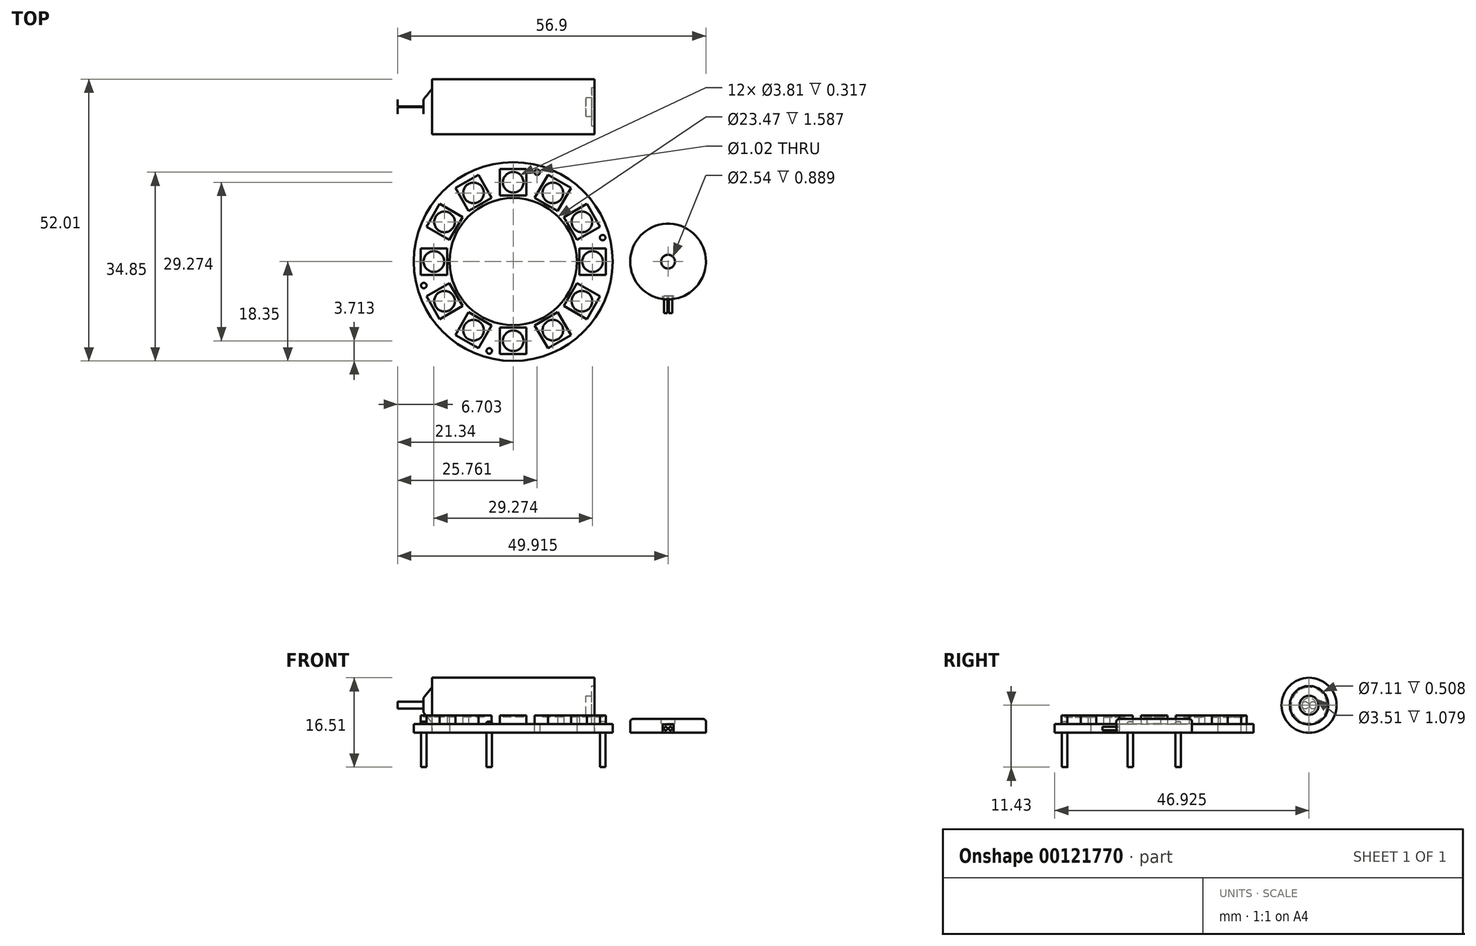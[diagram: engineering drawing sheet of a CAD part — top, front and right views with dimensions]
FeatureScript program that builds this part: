
annotation { "Feature Type Name" : "Feature", "Feature Type Description" : "" }
export const myFeature = defineFeature(function(context is Context, id is Id, definition is map)
    precondition{}
    {
        {
            var Q0;
            Q0=qCreatedBy(makeId("Top.planeOp"),FACE);
            var sketch = newSketch(context, id + "F0", { "sketchPlane" : qUnion([Q0])});
            skCircle(sketch, "E0", {"center": v(0, 0) * mm, "radius": 18.35 * mm});
            skCircle(sketch, "E1", {"center": v(0, 0) * mm, "radius": 11.73 * mm});
            skLineSegment(sketch, "E2", {"start": v(0, 0) * mm, "end": v(0, 18.35) * mm, "construction": true});
            skLineSegment(sketch, "E3.1.0", {"start": v(0, 0) * mm, "end": v(-4.75, 17.73) * mm, "construction": true});
            skLineSegment(sketch, "E3.2.0", {"start": v(0, 0) * mm, "end": v(-9.18, 15.9) * mm, "construction": true});
            skLineSegment(sketch, "E3.3.0", {"start": v(0, 0) * mm, "end": v(-12.98, 12.98) * mm, "construction": true});
            skLineSegment(sketch, "E3.4.0", {"start": v(0, 0) * mm, "end": v(-15.9, 9.18) * mm, "construction": true});
            skLineSegment(sketch, "E3.5.0", {"start": v(0, 0) * mm, "end": v(-17.73, 4.75) * mm, "construction": true});
            skLineSegment(sketch, "E3.6.0", {"start": v(0, 0) * mm, "end": v(-18.35, 0) * mm, "construction": true});
            skLineSegment(sketch, "E3.7.0", {"start": v(0, 0) * mm, "end": v(-17.73, -4.75) * mm, "construction": true});
            skLineSegment(sketch, "E3.8.0", {"start": v(0, 0) * mm, "end": v(-15.9, -9.18) * mm, "construction": true});
            skLineSegment(sketch, "E3.9.0", {"start": v(0, 0) * mm, "end": v(-12.98, -12.98) * mm, "construction": true});
            skLineSegment(sketch, "E3.10.0", {"start": v(0, 0) * mm, "end": v(-9.18, -15.9) * mm, "construction": true});
            skLineSegment(sketch, "E3.11.0", {"start": v(0, 0) * mm, "end": v(-4.75, -17.73) * mm, "construction": true});
            skLineSegment(sketch, "E3.12.0", {"start": v(0, 0) * mm, "end": v(0, -18.35) * mm, "construction": true});
            skLineSegment(sketch, "E3.13.0", {"start": v(0, 0) * mm, "end": v(4.75, -17.73) * mm, "construction": true});
            skLineSegment(sketch, "E3.14.0", {"start": v(0, 0) * mm, "end": v(9.18, -15.9) * mm, "construction": true});
            skLineSegment(sketch, "E3.15.0", {"start": v(0, 0) * mm, "end": v(12.98, -12.98) * mm, "construction": true});
            skLineSegment(sketch, "E3.16.0", {"start": v(0, 0) * mm, "end": v(15.9, -9.18) * mm, "construction": true});
            skLineSegment(sketch, "E3.17.0", {"start": v(0, 0) * mm, "end": v(17.73, -4.75) * mm, "construction": true});
            skLineSegment(sketch, "E3.18.0", {"start": v(0, 0) * mm, "end": v(18.35, 0) * mm, "construction": true});
            skLineSegment(sketch, "E3.19.0", {"start": v(0, 0) * mm, "end": v(17.73, 4.75) * mm, "construction": true});
            skLineSegment(sketch, "E3.20.0", {"start": v(0, 0) * mm, "end": v(15.9, 9.18) * mm, "construction": true});
            skLineSegment(sketch, "E3.21.0", {"start": v(0, 0) * mm, "end": v(12.98, 12.98) * mm, "construction": true});
            skLineSegment(sketch, "E3.22.0", {"start": v(0, 0) * mm, "end": v(9.18, 15.9) * mm, "construction": true});
            skLineSegment(sketch, "E3.23.0", {"start": v(0, 0) * mm, "end": v(4.75, 17.73) * mm, "construction": true});
            skCircle(sketch, "E4", {"center": v(4.42, 16.5) * mm, "radius": 0.5 * mm});
            skCircle(sketch, "E5", {"center": v(16.5, 4.42) * mm, "radius": 0.5 * mm});
            skCircle(sketch, "E6", {"center": v(-16.5, -4.42) * mm, "radius": 0.5 * mm});
            skCircle(sketch, "E7", {"center": v(-4.42, -16.5) * mm, "radius": 0.5 * mm});
            skSolve(sketch);
        }
        {
            var Q0;
            Q0=makeQuery(id+"F0.imprint","IMPRINT",FACE,{"disambiguationData":[TD([[makeQuery(id+"F0.imprint","IMPRINT",EDGE,{"derivedFrom":sQuery(id+"F0.wireOp",EDGE,"E0")}),1.0]])]});
            extrude(context, id + "F1", {"entities" : qUnion([Q0]), "depth" : 1.59 * mm});
        }
        {
            var Q0;
            Q0=makeQuery(id+"F1.opExtrude","CAP_FACE",FACE,{"disambiguationData":[OSD([sQuery(id+"F0.wireOp",EDGE,"E0"),sQuery(id+"F0.wireOp",EDGE,"E1"),sQuery(id+"F0.wireOp",EDGE,"E4"),sQuery(id+"F0.wireOp",EDGE,"E5"),sQuery(id+"F0.wireOp",EDGE,"E6"),sQuery(id+"F0.wireOp",EDGE,"E7")])],"isStart":false});
            var sketch = newSketch(context, id + "F2", { "sketchPlane" : qUnion([Q0])});
            skLineSegment(sketch, "E8.bottom", {"start": v(-2.44, 17.08) * mm, "end": v(2.44, 17.08) * mm});
            skLineSegment(sketch, "E8.top", {"start": v(-2.44, 12.2) * mm, "end": v(2.44, 12.2) * mm});
            skLineSegment(sketch, "E8.left", {"start": v(-2.44, 17.08) * mm, "end": v(-2.44, 12.2) * mm});
            skLineSegment(sketch, "E8.right", {"start": v(2.44, 17.08) * mm, "end": v(2.44, 12.2) * mm});
            skCircle(sketch, "E9", {"center": v(0, 14.64) * mm, "radius": 1.9 * mm});
            skPoint(sketch, "E9.centerSnap0", {"position": v(-2.44, 14.64) * mm});
            skCircle(sketch, "E10.1.0", {"center": v(-7.32, 12.68) * mm, "radius": 1.9 * mm});
            skLineSegment(sketch, "E10.1.1", {"start": v(-10.66, 13.57) * mm, "end": v(-6.42, 16.02) * mm});
            skLineSegment(sketch, "E10.1.2", {"start": v(-6.42, 16.02) * mm, "end": v(-3.98, 11.78) * mm});
            skLineSegment(sketch, "E10.1.3", {"start": v(-8.21, 9.34) * mm, "end": v(-3.98, 11.78) * mm});
            skLineSegment(sketch, "E10.1.4", {"start": v(-10.66, 13.57) * mm, "end": v(-8.21, 9.34) * mm});
            skCircle(sketch, "E10.2.0", {"center": v(-12.68, 7.32) * mm, "radius": 1.9 * mm});
            skLineSegment(sketch, "E10.2.1", {"start": v(-16.02, 6.42) * mm, "end": v(-13.57, 10.66) * mm});
            skLineSegment(sketch, "E10.2.2", {"start": v(-13.57, 10.66) * mm, "end": v(-9.34, 8.21) * mm});
            skLineSegment(sketch, "E10.2.3", {"start": v(-11.78, 3.98) * mm, "end": v(-9.34, 8.21) * mm});
            skLineSegment(sketch, "E10.2.4", {"start": v(-16.02, 6.42) * mm, "end": v(-11.78, 3.98) * mm});
            skCircle(sketch, "E10.3.0", {"center": v(-14.64, 0) * mm, "radius": 1.9 * mm});
            skLineSegment(sketch, "E10.3.1", {"start": v(-17.08, -2.44) * mm, "end": v(-17.08, 2.44) * mm});
            skLineSegment(sketch, "E10.3.2", {"start": v(-17.08, 2.44) * mm, "end": v(-12.2, 2.44) * mm});
            skLineSegment(sketch, "E10.3.3", {"start": v(-12.2, -2.44) * mm, "end": v(-12.2, 2.44) * mm});
            skLineSegment(sketch, "E10.3.4", {"start": v(-17.08, -2.44) * mm, "end": v(-12.2, -2.44) * mm});
            skCircle(sketch, "E10.4.0", {"center": v(-12.68, -7.32) * mm, "radius": 1.9 * mm});
            skLineSegment(sketch, "E10.4.1", {"start": v(-13.57, -10.66) * mm, "end": v(-16.02, -6.42) * mm});
            skLineSegment(sketch, "E10.4.2", {"start": v(-16.02, -6.42) * mm, "end": v(-11.78, -3.98) * mm});
            skLineSegment(sketch, "E10.4.3", {"start": v(-9.34, -8.21) * mm, "end": v(-11.78, -3.98) * mm});
            skLineSegment(sketch, "E10.4.4", {"start": v(-13.57, -10.66) * mm, "end": v(-9.34, -8.21) * mm});
            skCircle(sketch, "E10.5.0", {"center": v(-7.32, -12.68) * mm, "radius": 1.9 * mm});
            skLineSegment(sketch, "E10.5.1", {"start": v(-6.42, -16.02) * mm, "end": v(-10.66, -13.57) * mm});
            skLineSegment(sketch, "E10.5.2", {"start": v(-10.66, -13.57) * mm, "end": v(-8.21, -9.34) * mm});
            skLineSegment(sketch, "E10.5.3", {"start": v(-3.98, -11.78) * mm, "end": v(-8.21, -9.34) * mm});
            skLineSegment(sketch, "E10.5.4", {"start": v(-6.42, -16.02) * mm, "end": v(-3.98, -11.78) * mm});
            skCircle(sketch, "E10.6.0", {"center": v(0, -14.64) * mm, "radius": 1.9 * mm});
            skLineSegment(sketch, "E10.6.1", {"start": v(2.44, -17.08) * mm, "end": v(-2.44, -17.08) * mm});
            skLineSegment(sketch, "E10.6.2", {"start": v(-2.44, -17.08) * mm, "end": v(-2.44, -12.2) * mm});
            skLineSegment(sketch, "E10.6.3", {"start": v(2.44, -12.2) * mm, "end": v(-2.44, -12.2) * mm});
            skLineSegment(sketch, "E10.6.4", {"start": v(2.44, -17.08) * mm, "end": v(2.44, -12.2) * mm});
            skCircle(sketch, "E10.7.0", {"center": v(7.32, -12.68) * mm, "radius": 1.9 * mm});
            skLineSegment(sketch, "E10.7.1", {"start": v(10.66, -13.57) * mm, "end": v(6.42, -16.02) * mm});
            skLineSegment(sketch, "E10.7.2", {"start": v(6.42, -16.02) * mm, "end": v(3.98, -11.78) * mm});
            skLineSegment(sketch, "E10.7.3", {"start": v(8.21, -9.34) * mm, "end": v(3.98, -11.78) * mm});
            skLineSegment(sketch, "E10.7.4", {"start": v(10.66, -13.57) * mm, "end": v(8.21, -9.34) * mm});
            skCircle(sketch, "E10.8.0", {"center": v(12.68, -7.32) * mm, "radius": 1.9 * mm});
            skLineSegment(sketch, "E10.8.1", {"start": v(16.02, -6.42) * mm, "end": v(13.57, -10.66) * mm});
            skLineSegment(sketch, "E10.8.2", {"start": v(13.57, -10.66) * mm, "end": v(9.34, -8.21) * mm});
            skLineSegment(sketch, "E10.8.3", {"start": v(11.78, -3.98) * mm, "end": v(9.34, -8.21) * mm});
            skLineSegment(sketch, "E10.8.4", {"start": v(16.02, -6.42) * mm, "end": v(11.78, -3.98) * mm});
            skCircle(sketch, "E10.9.0", {"center": v(14.64, 0) * mm, "radius": 1.9 * mm});
            skLineSegment(sketch, "E10.9.1", {"start": v(17.08, 2.44) * mm, "end": v(17.08, -2.44) * mm});
            skLineSegment(sketch, "E10.9.2", {"start": v(17.08, -2.44) * mm, "end": v(12.2, -2.44) * mm});
            skLineSegment(sketch, "E10.9.3", {"start": v(12.2, 2.44) * mm, "end": v(12.2, -2.44) * mm});
            skLineSegment(sketch, "E10.9.4", {"start": v(17.08, 2.44) * mm, "end": v(12.2, 2.44) * mm});
            skCircle(sketch, "E10.10.0", {"center": v(12.68, 7.32) * mm, "radius": 1.9 * mm});
            skLineSegment(sketch, "E10.10.1", {"start": v(13.57, 10.66) * mm, "end": v(16.02, 6.42) * mm});
            skLineSegment(sketch, "E10.10.2", {"start": v(16.02, 6.42) * mm, "end": v(11.78, 3.98) * mm});
            skLineSegment(sketch, "E10.10.3", {"start": v(9.34, 8.21) * mm, "end": v(11.78, 3.98) * mm});
            skLineSegment(sketch, "E10.10.4", {"start": v(13.57, 10.66) * mm, "end": v(9.34, 8.21) * mm});
            skCircle(sketch, "E10.11.0", {"center": v(7.32, 12.68) * mm, "radius": 1.9 * mm});
            skLineSegment(sketch, "E10.11.1", {"start": v(6.42, 16.02) * mm, "end": v(10.66, 13.57) * mm});
            skLineSegment(sketch, "E10.11.2", {"start": v(10.66, 13.57) * mm, "end": v(8.21, 9.34) * mm});
            skLineSegment(sketch, "E10.11.3", {"start": v(3.98, 11.78) * mm, "end": v(8.21, 9.34) * mm});
            skLineSegment(sketch, "E10.11.4", {"start": v(6.42, 16.02) * mm, "end": v(3.98, 11.78) * mm});
            skPoint(sketch, "E10.center", {"position": v(0, 0) * mm});
            skSolve(sketch);
        }
        {
            var Q0;
            Q0=qSketchRegion(id+"F2",true);
            extrude(context, id + "F3", {"entities" : qUnion([Q0]), "operationType" : NewBodyOperationType.ADD, "depth" : 1.59 * mm});
        }
        {
            var Q0;
            Q0=makeQuery(id+"F3.boolean.opBoolean","SPLIT",FACE,{"disambiguationData":[TD([makeQuery(id+"F3.opExtrude","SWEPT_FACE",FACE,{"disambiguationData":[OSD([sQuery(id+"F2.wireOp",EDGE,"E9")])]})])],"derivedFrom":makeQuery(id+"F1.opExtrude","CAP_FACE",FACE,{"disambiguationData":[OSD([sQuery(id+"F0.wireOp",EDGE,"E0"),sQuery(id+"F0.wireOp",EDGE,"E1"),sQuery(id+"F0.wireOp",EDGE,"E4"),sQuery(id+"F0.wireOp",EDGE,"E5"),sQuery(id+"F0.wireOp",EDGE,"E6"),sQuery(id+"F0.wireOp",EDGE,"E7")])],"isStart":false})});
            var Q1;
            Q1=makeQuery(id+"F3.boolean.opBoolean","SPLIT",FACE,{"disambiguationData":[TD([makeQuery(id+"F3.opExtrude","SWEPT_FACE",FACE,{"disambiguationData":[OSD([sQuery(id+"F2.wireOp",EDGE,"E10.11.0")])]})])],"derivedFrom":makeQuery(id+"F1.opExtrude","CAP_FACE",FACE,{"disambiguationData":[OSD([sQuery(id+"F0.wireOp",EDGE,"E0"),sQuery(id+"F0.wireOp",EDGE,"E1"),sQuery(id+"F0.wireOp",EDGE,"E4"),sQuery(id+"F0.wireOp",EDGE,"E5"),sQuery(id+"F0.wireOp",EDGE,"E6"),sQuery(id+"F0.wireOp",EDGE,"E7")])],"isStart":false})});
            var Q2;
            Q2=makeQuery(id+"F3.boolean.opBoolean","SPLIT",FACE,{"disambiguationData":[TD([makeQuery(id+"F3.opExtrude","SWEPT_FACE",FACE,{"disambiguationData":[OSD([sQuery(id+"F2.wireOp",EDGE,"E10.10.0")])]})])],"derivedFrom":makeQuery(id+"F1.opExtrude","CAP_FACE",FACE,{"disambiguationData":[OSD([sQuery(id+"F0.wireOp",EDGE,"E0"),sQuery(id+"F0.wireOp",EDGE,"E1"),sQuery(id+"F0.wireOp",EDGE,"E4"),sQuery(id+"F0.wireOp",EDGE,"E5"),sQuery(id+"F0.wireOp",EDGE,"E6"),sQuery(id+"F0.wireOp",EDGE,"E7")])],"isStart":false})});
            var Q3;
            Q3=makeQuery(id+"F3.boolean.opBoolean","SPLIT",FACE,{"disambiguationData":[TD([makeQuery(id+"F3.opExtrude","SWEPT_FACE",FACE,{"disambiguationData":[OSD([sQuery(id+"F2.wireOp",EDGE,"E10.9.0")])]})])],"derivedFrom":makeQuery(id+"F1.opExtrude","CAP_FACE",FACE,{"disambiguationData":[OSD([sQuery(id+"F0.wireOp",EDGE,"E0"),sQuery(id+"F0.wireOp",EDGE,"E1"),sQuery(id+"F0.wireOp",EDGE,"E4"),sQuery(id+"F0.wireOp",EDGE,"E5"),sQuery(id+"F0.wireOp",EDGE,"E6"),sQuery(id+"F0.wireOp",EDGE,"E7")])],"isStart":false})});
            var Q4;
            Q4=makeQuery(id+"F3.boolean.opBoolean","SPLIT",FACE,{"disambiguationData":[TD([makeQuery(id+"F3.opExtrude","SWEPT_FACE",FACE,{"disambiguationData":[OSD([sQuery(id+"F2.wireOp",EDGE,"E10.8.0")])]})])],"derivedFrom":makeQuery(id+"F1.opExtrude","CAP_FACE",FACE,{"disambiguationData":[OSD([sQuery(id+"F0.wireOp",EDGE,"E0"),sQuery(id+"F0.wireOp",EDGE,"E1"),sQuery(id+"F0.wireOp",EDGE,"E4"),sQuery(id+"F0.wireOp",EDGE,"E5"),sQuery(id+"F0.wireOp",EDGE,"E6"),sQuery(id+"F0.wireOp",EDGE,"E7")])],"isStart":false})});
            var Q5;
            Q5=makeQuery(id+"F3.boolean.opBoolean","SPLIT",FACE,{"disambiguationData":[TD([makeQuery(id+"F3.opExtrude","SWEPT_FACE",FACE,{"disambiguationData":[OSD([sQuery(id+"F2.wireOp",EDGE,"E10.7.0")])]})])],"derivedFrom":makeQuery(id+"F1.opExtrude","CAP_FACE",FACE,{"disambiguationData":[OSD([sQuery(id+"F0.wireOp",EDGE,"E0"),sQuery(id+"F0.wireOp",EDGE,"E1"),sQuery(id+"F0.wireOp",EDGE,"E4"),sQuery(id+"F0.wireOp",EDGE,"E5"),sQuery(id+"F0.wireOp",EDGE,"E6"),sQuery(id+"F0.wireOp",EDGE,"E7")])],"isStart":false})});
            var Q6;
            Q6=makeQuery(id+"F3.boolean.opBoolean","SPLIT",FACE,{"disambiguationData":[TD([makeQuery(id+"F3.opExtrude","SWEPT_FACE",FACE,{"disambiguationData":[OSD([sQuery(id+"F2.wireOp",EDGE,"E10.6.0")])]})])],"derivedFrom":makeQuery(id+"F1.opExtrude","CAP_FACE",FACE,{"disambiguationData":[OSD([sQuery(id+"F0.wireOp",EDGE,"E0"),sQuery(id+"F0.wireOp",EDGE,"E1"),sQuery(id+"F0.wireOp",EDGE,"E4"),sQuery(id+"F0.wireOp",EDGE,"E5"),sQuery(id+"F0.wireOp",EDGE,"E6"),sQuery(id+"F0.wireOp",EDGE,"E7")])],"isStart":false})});
            var Q7;
            Q7=makeQuery(id+"F3.boolean.opBoolean","SPLIT",FACE,{"disambiguationData":[TD([makeQuery(id+"F3.opExtrude","SWEPT_FACE",FACE,{"disambiguationData":[OSD([sQuery(id+"F2.wireOp",EDGE,"E10.5.0")])]})])],"derivedFrom":makeQuery(id+"F1.opExtrude","CAP_FACE",FACE,{"disambiguationData":[OSD([sQuery(id+"F0.wireOp",EDGE,"E0"),sQuery(id+"F0.wireOp",EDGE,"E1"),sQuery(id+"F0.wireOp",EDGE,"E4"),sQuery(id+"F0.wireOp",EDGE,"E5"),sQuery(id+"F0.wireOp",EDGE,"E6"),sQuery(id+"F0.wireOp",EDGE,"E7")])],"isStart":false})});
            var Q8;
            Q8=makeQuery(id+"F3.boolean.opBoolean","SPLIT",FACE,{"disambiguationData":[TD([makeQuery(id+"F3.opExtrude","SWEPT_FACE",FACE,{"disambiguationData":[OSD([sQuery(id+"F2.wireOp",EDGE,"E10.4.0")])]})])],"derivedFrom":makeQuery(id+"F1.opExtrude","CAP_FACE",FACE,{"disambiguationData":[OSD([sQuery(id+"F0.wireOp",EDGE,"E0"),sQuery(id+"F0.wireOp",EDGE,"E1"),sQuery(id+"F0.wireOp",EDGE,"E4"),sQuery(id+"F0.wireOp",EDGE,"E5"),sQuery(id+"F0.wireOp",EDGE,"E6"),sQuery(id+"F0.wireOp",EDGE,"E7")])],"isStart":false})});
            var Q9;
            Q9=makeQuery(id+"F3.boolean.opBoolean","SPLIT",FACE,{"disambiguationData":[TD([makeQuery(id+"F3.opExtrude","SWEPT_FACE",FACE,{"disambiguationData":[OSD([sQuery(id+"F2.wireOp",EDGE,"E10.3.0")])]})])],"derivedFrom":makeQuery(id+"F1.opExtrude","CAP_FACE",FACE,{"disambiguationData":[OSD([sQuery(id+"F0.wireOp",EDGE,"E0"),sQuery(id+"F0.wireOp",EDGE,"E1"),sQuery(id+"F0.wireOp",EDGE,"E4"),sQuery(id+"F0.wireOp",EDGE,"E5"),sQuery(id+"F0.wireOp",EDGE,"E6"),sQuery(id+"F0.wireOp",EDGE,"E7")])],"isStart":false})});
            var Q10;
            Q10=makeQuery(id+"F3.boolean.opBoolean","SPLIT",FACE,{"disambiguationData":[TD([makeQuery(id+"F3.opExtrude","SWEPT_FACE",FACE,{"disambiguationData":[OSD([sQuery(id+"F2.wireOp",EDGE,"E10.2.0")])]})])],"derivedFrom":makeQuery(id+"F1.opExtrude","CAP_FACE",FACE,{"disambiguationData":[OSD([sQuery(id+"F0.wireOp",EDGE,"E0"),sQuery(id+"F0.wireOp",EDGE,"E1"),sQuery(id+"F0.wireOp",EDGE,"E4"),sQuery(id+"F0.wireOp",EDGE,"E5"),sQuery(id+"F0.wireOp",EDGE,"E6"),sQuery(id+"F0.wireOp",EDGE,"E7")])],"isStart":false})});
            var Q11;
            Q11=makeQuery(id+"F3.boolean.opBoolean","SPLIT",FACE,{"disambiguationData":[TD([makeQuery(id+"F3.opExtrude","SWEPT_FACE",FACE,{"disambiguationData":[OSD([sQuery(id+"F2.wireOp",EDGE,"E10.1.0")])]})])],"derivedFrom":makeQuery(id+"F1.opExtrude","CAP_FACE",FACE,{"disambiguationData":[OSD([sQuery(id+"F0.wireOp",EDGE,"E0"),sQuery(id+"F0.wireOp",EDGE,"E1"),sQuery(id+"F0.wireOp",EDGE,"E4"),sQuery(id+"F0.wireOp",EDGE,"E5"),sQuery(id+"F0.wireOp",EDGE,"E6"),sQuery(id+"F0.wireOp",EDGE,"E7")])],"isStart":false})});
            extrude(context, id + "F4", {"entities" : qUnion([Q0, Q1, Q2, Q3, Q4, Q5, Q6, Q7, Q8, Q9, Q10, Q11]), "operationType" : NewBodyOperationType.ADD, "depth" : 1.27 * mm});
        }
        {
            var Q0;
            Q0=makeQuery(id+"F0.imprint","IMPRINT",FACE,{"disambiguationData":[TD([[makeQuery(id+"F0.imprint","IMPRINT",EDGE,{"derivedFrom":sQuery(id+"F0.wireOp",EDGE,"E7")}),1.0]])]});
            var Q1;
            Q1=makeQuery(id+"F0.imprint","IMPRINT",FACE,{"disambiguationData":[TD([[makeQuery(id+"F0.imprint","IMPRINT",EDGE,{"derivedFrom":sQuery(id+"F0.wireOp",EDGE,"E6")}),1.0]])]});
            var Q2;
            Q2=makeQuery(id+"F0.imprint","IMPRINT",FACE,{"disambiguationData":[TD([[makeQuery(id+"F0.imprint","IMPRINT",EDGE,{"derivedFrom":sQuery(id+"F0.wireOp",EDGE,"E5")}),1.0]])]});
            extrude(context, id + "F5", {"entities" : qUnion([Q0, Q1, Q2]), "operationType" : NewBodyOperationType.ADD, "oppositeDirection" : true, "depth" : 6.35 * mm, "hasSecondDirection" : true, "secondDirectionOppositeDirection" : false, "secondDirectionDepth" : 2.03 * mm});
        }
        {
            var Q0;
            Q0=makeQuery(id+"F1.opExtrude","CAP_EDGE",EDGE,{"disambiguationData":[OSD([sQuery(id+"F0.wireOp",EDGE,"E5")])],"isStart":false});
            var Q1;
            Q1=makeQuery(id+"F5.opExtrude","CAP_EDGE",EDGE,{"disambiguationData":[OSD([sQuery(id+"F0.wireOp",EDGE,"E5")])],"isStart":true});
            var Q2;
            Q2=makeQuery(id+"F5.opExtrude","CAP_EDGE",EDGE,{"disambiguationData":[OSD([sQuery(id+"F0.wireOp",EDGE,"E6")])],"isStart":true});
            var Q3;
            Q3=makeQuery(id+"F5.opExtrude","CAP_EDGE",EDGE,{"disambiguationData":[OSD([sQuery(id+"F0.wireOp",EDGE,"E7")])],"isStart":true});
            var Q4;
            Q4=makeQuery(id+"F1.opExtrude","CAP_EDGE",EDGE,{"disambiguationData":[OSD([sQuery(id+"F0.wireOp",EDGE,"E6")])],"isStart":false});
            var Q5;
            Q5=makeQuery(id+"F1.opExtrude","CAP_EDGE",EDGE,{"disambiguationData":[OSD([sQuery(id+"F0.wireOp",EDGE,"E7")])],"isStart":false});
            fillet(context, id + "F6", {"entities" : qUnion([Q0, Q1, Q2, Q3, Q4, Q5]), "radius" : 0.2 * mm, "tangentPropagation" : true, "allowEdgeOverflow" : false});
        }
        {
            var Q0;
            Q0=qCreatedBy(makeId("Top.planeOp"),FACE);
            var sketch = newSketch(context, id + "F7", { "sketchPlane" : qUnion([Q0])});
            skCircle(sketch, "E11", {"center": v(28.58, 0) * mm, "radius": 6.99 * mm});
            skSolve(sketch);
        }
        {
            var Q0;
            Q0=makeQuery(id+"F7.imprint","IMPRINT",FACE,{"disambiguationData":[TD([[makeQuery(id+"F7.imprint","IMPRINT",EDGE,{"derivedFrom":sQuery(id+"F7.wireOp",EDGE,"E11")}),1.0]])]});
            extrude(context, id + "F8", {"entities" : qUnion([Q0]), "depth" : 2.54 * mm});
        }
        {
            var Q0;
            Q0=makeQuery(id+"F8.opExtrude","CAP_EDGE",EDGE,{"disambiguationData":[OSD([sQuery(id+"F7.wireOp",EDGE,"E11")])],"isStart":false});
            fillet(context, id + "F9", {"entities" : qUnion([Q0]), "radius" : 0.5 * mm, "tangentPropagation" : true, "allowEdgeOverflow" : false});
        }
        {
            var Q0;
            Q0=makeQuery(id+"F8.opExtrude","CAP_FACE",FACE,{"disambiguationData":[OSD([sQuery(id+"F7.wireOp",EDGE,"E11")])],"isStart":false});
            var sketch = newSketch(context, id + "F10", { "sketchPlane" : qUnion([Q0])});
            skCircle(sketch, "E12", {"center": v(28.58, 0) * mm, "radius": 1.27 * mm});
            skSolve(sketch);
        }
        {
            var Q0;
            Q0=makeQuery(id+"F10.imprint","IMPRINT",FACE,{"disambiguationData":[TD([[makeQuery(id+"F10.imprint","IMPRINT",EDGE,{"derivedFrom":sQuery(id+"F10.wireOp",EDGE,"E12")}),1.0]])]});
            extrude(context, id + "F11", {"entities" : qUnion([Q0]), "operationType" : NewBodyOperationType.REMOVE, "oppositeDirection" : true, "depth" : 0.89 * mm});
        }
        {
            var Q0;
            Q0=qCreatedBy(makeId("Front.planeOp"),FACE);
            var sketch = newSketch(context, id + "F12", { "sketchPlane" : qUnion([Q0])});
            skLineSegment(sketch, "E13", {"start": v(27.56, 0) * mm, "end": v(27.56, 1.52) * mm});
            skLineSegment(sketch, "E14", {"start": v(27.56, 1.52) * mm, "end": v(29.6, 1.52) * mm});
            skLineSegment(sketch, "E15", {"start": v(29.6, 1.52) * mm, "end": v(29.6, 0) * mm});
            skLineSegment(sketch, "E16", {"start": v(29.6, 0) * mm, "end": v(27.56, 0) * mm});
            skLineSegment(sketch, "E17.0", {"start": v(21.59, 0) * mm, "end": v(35.56, 0) * mm, "construction": true});
            skPoint(sketch, "E18", {"position": v(28.58, 0) * mm});
            skSolve(sketch);
        }
        {
            var Q0;
            Q0=qSketchRegion(id+"F12",true);
            extrude(context, id + "F13", {"entities" : qUnion([Q0]), "operationType" : NewBodyOperationType.REMOVE, "depth" : 7.62 * mm, "hasSecondDirection" : true, "secondDirectionOppositeDirection" : false, "secondDirectionDepth" : 6.35 * mm});
        }
        {
            var Q0;
            Q0=makeQuery(id+"F13.boolean.opBoolean","COPY",FACE,{"derivedFrom":makeQuery(id+"F13.opExtrude","CAP_FACE",FACE,{"disambiguationData":[OSD([sQuery(id+"F12.wireOp",EDGE,"E13"),sQuery(id+"F12.wireOp",EDGE,"E14"),sQuery(id+"F12.wireOp",EDGE,"E15"),sQuery(id+"F12.wireOp",EDGE,"E16")])],"isStart":true})});
            var sketch = newSketch(context, id + "F14", { "sketchPlane" : qUnion([Q0])});
            skCircle(sketch, "E19", {"center": v(28.13, 0.76) * mm, "radius": 0.32 * mm});
            skPoint(sketch, "E19.centerSnap0", {"position": v(27.56, 0.76) * mm});
            skCircle(sketch, "E20", {"center": v(29.02, 0.76) * mm, "radius": 0.32 * mm});
            skLineSegment(sketch, "E21", {"start": v(28.13, 0.76) * mm, "end": v(29.02, 0.76) * mm, "construction": true});
            skLineSegment(sketch, "E22", {"start": v(28.58, 0.76) * mm, "end": v(28.58, 1.52) * mm, "construction": true});
            skSolve(sketch);
        }
        {
            var Q0;
            Q0=makeQuery(id+"F14.imprint","IMPRINT",FACE,{"disambiguationData":[TD([[makeQuery(id+"F14.imprint","IMPRINT",EDGE,{"derivedFrom":sQuery(id+"F14.wireOp",EDGE,"E19")}),1.0]])]});
            var Q1;
            Q1=makeQuery(id+"F14.imprint","IMPRINT",FACE,{"disambiguationData":[TD([[makeQuery(id+"F14.imprint","IMPRINT",EDGE,{"derivedFrom":sQuery(id+"F14.wireOp",EDGE,"E20")}),1.0]])]});
            extrude(context, id + "F15", {"entities" : qUnion([Q0, Q1]), "operationType" : NewBodyOperationType.ADD, "depth" : 3.17 * mm});
        }
        {
            var Q0;
            Q0=qCreatedBy(makeId("Right.planeOp"),FACE);
            var sketch = newSketch(context, id + "F16", { "sketchPlane" : qUnion([Q0])});
            skCircle(sketch, "E23", {"center": v(28.58, 5.08) * mm, "radius": 5.08 * mm});
            skLineSegment(sketch, "E24", {"start": v(0, 0) * mm, "end": v(28.57, 0) * mm, "construction": true});
            skSolve(sketch);
        }
        {
            var Q0;
            Q0=makeQuery(id+"F16.imprint","IMPRINT",FACE,{"disambiguationData":[TD([[makeQuery(id+"F16.imprint","IMPRINT",EDGE,{"derivedFrom":sQuery(id+"F16.wireOp",EDGE,"E23")}),1.0]])]});
            extrude(context, id + "F17", {"entities" : qUnion([Q0]), "endBound" : BoundingType.SYMMETRIC, "depth" : 29.97 * mm});
        }
        {
            var Q0;
            Q0=makeQuery(id+"F17.opExtrude","CAP_FACE",FACE,{"disambiguationData":[OSD([sQuery(id+"F16.wireOp",EDGE,"E23")])],"isStart":false});
            var sketch = newSketch(context, id + "F18", { "sketchPlane" : qUnion([Q0])});
            skCircle(sketch, "E25", {"center": v(28.58, 5.08) * mm, "radius": 1.75 * mm});
            skCircle(sketch, "E26", {"center": v(28.58, 5.08) * mm, "radius": 3.56 * mm});
            skSolve(sketch);
        }
        {
            var Q0;
            Q0=makeQuery(id+"F18.imprint","IMPRINT",FACE,{"disambiguationData":[TD([[makeQuery(id+"F18.imprint","IMPRINT",EDGE,{"derivedFrom":sQuery(id+"F18.wireOp",EDGE,"E25")}),1.0]])]});
            extrude(context, id + "F19", {"entities" : qUnion([Q0]), "operationType" : NewBodyOperationType.REMOVE, "oppositeDirection" : true, "depth" : 1.59 * mm});
        }
        {
            var Q0;
            Q0=makeQuery(id+"F18.imprint","IMPRINT",FACE,{"disambiguationData":[TD([[makeQuery(id+"F18.imprint","IMPRINT",EDGE,{"derivedFrom":sQuery(id+"F18.wireOp",EDGE,"E25")}),-1.0]])]});
            extrude(context, id + "F20", {"entities" : qUnion([Q0]), "operationType" : NewBodyOperationType.REMOVE, "oppositeDirection" : true, "depth" : 0.5 * mm});
        }
        {
            var Q0;
            Q0=makeQuery(id+"F17.opExtrude","CAP_FACE",FACE,{"disambiguationData":[OSD([sQuery(id+"F16.wireOp",EDGE,"E23")])],"isStart":true});
            var sketch = newSketch(context, id + "F21", { "sketchPlane" : qUnion([Q0])});
            skCircle(sketch, "E27.0", {"center": v(-28.58, 5.08) * mm, "radius": 5.08 * mm, "construction": true});
            skCircle(sketch, "E28", {"center": v(-27.88, 5.08) * mm, "radius": 0.64 * mm});
            skCircle(sketch, "E29", {"center": v(-29.27, 5.08) * mm, "radius": 0.64 * mm});
            skLineSegment(sketch, "E30", {"start": v(-29.27, 5.08) * mm, "end": v(-27.88, 5.08) * mm, "construction": true});
            skSolve(sketch);
        }
        {
            var Q0;
            Q0=makeQuery(id+"F21.imprint","IMPRINT",FACE,{"disambiguationData":[TD([[makeQuery(id+"F21.imprint","IMPRINT",EDGE,{"derivedFrom":sQuery(id+"F21.wireOp",EDGE,"E29")}),1.0]])]});
            var Q1;
            Q1=makeQuery(id+"F21.imprint","IMPRINT",FACE,{"disambiguationData":[TD([[makeQuery(id+"F21.imprint","IMPRINT",EDGE,{"derivedFrom":sQuery(id+"F21.wireOp",EDGE,"E28")}),1.0]])]});
            extrude(context, id + "F22", {"entities" : qUnion([Q0, Q1]), "operationType" : NewBodyOperationType.ADD, "depth" : 6.35 * mm});
        }
        {
            var Q0;
            Q0=qCreatedBy(makeId("Top.planeOp"),FACE);
            cPlane(context, id + "F23", {"entities" : qUnion([Q0]), "cplaneType" : CPlaneType.OFFSET, "offset" : 5.08 * mm, "width" : 152.4 * mm, "height" : 152.4 * mm});
        }
        {
            var Q0;
            Q0=qCreatedBy(id+"F23.planeOp",FACE);
            var sketch = newSketch(context, id + "F24", { "sketchPlane" : qUnion([Q0])});
            skLineSegment(sketch, "E31", {"start": v(-16.57, 28.58) * mm, "end": v(-16.57, 29.9) * mm});
            skLineSegment(sketch, "E32.0", {"start": v(-14.99, 33.66) * mm, "end": v(-14.99, 23.5) * mm});
            skLineSegment(sketch, "E33", {"start": v(-16.57, 29.9) * mm, "end": v(-14.99, 31.88) * mm});
            skLineSegment(sketch, "E34", {"start": v(-16.57, 28.58) * mm, "end": v(-14.99, 28.58) * mm});
            skSolve(sketch);
        }
        {
            var Q0;
            Q0=makeQuery(id+"F24.imprint","IMPRINT",FACE,{"disambiguationData":[TD([[makeQuery(id+"F24.imprint","IMPRINT",EDGE,{"derivedFrom":sQuery(id+"F24.wireOp",EDGE,"E31")}),-1.0]])]});
            var Q1;
            Q1=sQuery(id+"F24.wireOp",EDGE,"E34");
            revolve(context, id + "F25", {"operationType" : NewBodyOperationType.ADD, "entities" : qUnion([Q0]), "axis" : qUnion([Q1]), "revolveType" : RevolveType.FULL});
        }
    });
